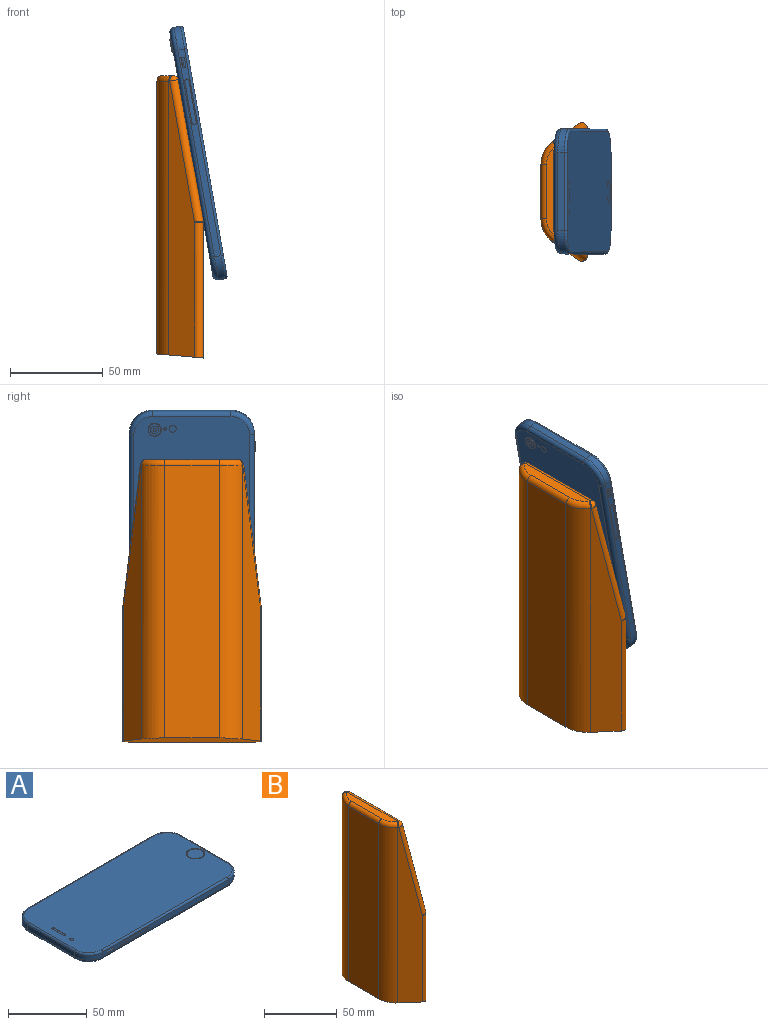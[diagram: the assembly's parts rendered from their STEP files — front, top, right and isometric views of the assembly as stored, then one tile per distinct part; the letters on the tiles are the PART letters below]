
ASSEMBLY  parts=2 mates=1
PART A: 109 faces, bbox 140.3x69.5x8.2 mm
  f0: plane 1.73x1.71mm, normal (0,0,-1), area 2.3mm2, adj f1,f2
  f1: cylinder r=0.86mm len=1.71mm, axis (0,0,-1), area 0mm2, adj f0,f2
  f2: plane 4.33x4.27mm, normal (0,0,-1), area 12mm2, adj f0,f1,f44
  f3: plane 5.31x0.85mm, normal (0,-1,0), area 4.4mm2, adj f7,f8,f9,f10,f11,f12,f13,f14
  f4: plane 10.67x10.67mm, normal (0,0,1), area 89.4mm2, adj f17
  f5: plane 2.46x2.46mm, normal (0,0,1), area 4.8mm2, adj f18
  f6: plane 11.48x1.4mm, normal (0,0,1), area 15.6mm2, adj f19,f20,f21,f22
  f7: cylinder r=0.23mm len=1.75mm, axis (0,-1,0), area 0.6mm2, adj f3,f8,f14,f23
  f8: plane 1.75x0.39mm, normal (-1,0,0), area 0.7mm2, adj f3,f7,f9,f23
  f9: cylinder r=0.23mm len=1.75mm, axis (0,-1,0), area 0.6mm2, adj f3,f8,f10,f23
  f10: plane 4.85x1.75mm, normal (0,0,-1), area 8.5mm2, adj f3,f9,f11,f23
  f11: cylinder r=0.23mm len=1.75mm, axis (0,-1,0), area 0.6mm2, adj f3,f10,f12,f23
  f12: plane 1.75x0.39mm, normal (1,0,0), area 0.7mm2, adj f3,f11,f13,f23
  f13: cylinder r=0.23mm len=1.75mm, axis (0,-1,0), area 0.6mm2, adj f3,f12,f14,f23
  f14: plane 4.85x1.75mm, normal (0,0,1), area 8.5mm2, adj f3,f7,f13,f23
  f15: plane 24.68x2.26mm, normal (0,-1,0), area 54.6mm2, adj f24,f25,f26,f27
  f16: plane 8.81x2.9mm, normal (1,0,0), area 23.7mm2, adj f37,f38,f39,f40
  f17: torus R=5.87mm, axis (0,0,1), area 19.8mm2, adj f4,f43
  f18: cylinder r=1.23mm len=2.46mm, axis (0,0,1), area 0mm2, adj f5,f43
  f19: torus R=0.9mm, axis (0,0,-1), area 0.8mm2, adj f6,f20,f22,f43
  f20: cylinder r=0.2mm len=10.08mm, axis (0,-1,0), area 3.2mm2, adj f6,f19,f21,f43
  f21: torus R=0.9mm, axis (0,0,-1), area 0.8mm2, adj f6,f20,f22,f43
  f22: cylinder r=0.2mm len=10.08mm, axis (0,1,0), area 3.2mm2, adj f6,f19,f21,f43
  f23: plane 5.51x1.89mm, normal (0,-1,0), area 6mm2, adj f7,f8,f9,f10,f11,f12,f13,f14
  f24: cylinder r=0.08mm len=22.42mm, axis (-1,0,0), area 2.7mm2, adj f15,f25,f27,f53
  f25: torus R=1.13mm, axis (0,1,0), area 0.4mm2, adj f15,f24,f26,f54
  f26: cylinder r=0.08mm len=22.42mm, axis (1,0,0), area 2.7mm2, adj f15,f25,f27,f55
  f27: torus R=1.13mm, axis (0,1,0), area 0.4mm2, adj f15,f24,f26,f56
  f28: plane 3.3x3.3mm, normal (1,0,0), area 8.6mm2, adj f60
  f29: plane 1.22x1.22mm, normal (1,0,0), area 1.2mm2, adj f61
  f30: plane 1.22x1.22mm, normal (1,0,0), area 1.2mm2, adj f62
  f31: plane 1.22x1.22mm, normal (1,0,0), area 1.2mm2, adj f63
  f32: plane 1.22x1.22mm, normal (1,0,0), area 1.2mm2, adj f64
  f33: plane 1.22x1.22mm, normal (1,0,0), area 1.2mm2, adj f65
  f34: plane 1.19x1.19mm, normal (1,0,0), area 1.1mm2, adj f66
  f35: plane 1.19x1.19mm, normal (1,0,0), area 1.1mm2, adj f67
  f36: plane 1.14x1.14mm, normal (1,0,0), area 1mm2, adj f68
  f37: plane 7.71x5.92mm, normal (0,0,1), area 45.6mm2, adj f16,f38,f40,f69
  f38: cylinder r=1.45mm len=7.71mm, axis (-1,0,0), area 35.1mm2, adj f16,f37,f39,f70
  f39: plane 7.71x5.92mm, normal (0,0,-1), area 45.6mm2, adj f16,f38,f40,f71
  f40: cylinder r=1.45mm len=7.71mm, axis (-1,0,0), area 35.1mm2, adj f16,f37,f39,f72
  f41: plane 1.22x1.22mm, normal (1,0,0), area 1.2mm2, adj f73
  f42: plane 11.58x2.61mm, normal (0,1,0), area 28.7mm2, adj f75,f76,f77,f78
  f43: plane 135.69x64.87mm, normal (0,0,1), area 8558.8mm2, adj f17,f18,f19,f20,f21,f22,f57,f58
  f44: plane 6.71x6.71mm, normal (0,0,-1), area 21mm2, adj f2,f83
  f45: plane 5.05x1.27mm, normal (0,0,-1), area 6.4mm2, adj f23,f46,f52,f84
  f46: cylinder r=0.23mm len=1.27mm, axis (0,1,0), area 0.5mm2, adj f23,f45,f47,f84
  f47: plane 1.44x1.27mm, normal (-1,0,0), area 1.8mm2, adj f23,f46,f48,f84
  f48: cylinder r=0.23mm len=1.27mm, axis (0,1,0), area 0.5mm2, adj f23,f47,f49,f84
  f49: plane 5.05x1.27mm, normal (0,0,1), area 6.4mm2, adj f23,f48,f50,f84
  f50: cylinder r=0.23mm len=1.27mm, axis (0,1,0), area 0.5mm2, adj f23,f49,f51,f84
  f51: plane 1.44x1.27mm, normal (1,0,0), area 1.8mm2, adj f23,f50,f52,f84
  f52: cylinder r=0.23mm len=1.27mm, axis (0,1,0), area 0.5mm2, adj f23,f45,f51,f84
  f53: plane 22.42x0.08mm, normal (0,0,1), area 1.7mm2, adj f24,f54,f56,f84
  f54: cylinder r=1.21mm len=2.41mm, axis (0,1,0), area 0.3mm2, adj f25,f53,f55,f84
  f55: plane 22.42x0.08mm, normal (0,0,-1), area 1.7mm2, adj f26,f54,f56,f84
  f56: cylinder r=1.2mm len=2.4mm, axis (0,1,0), area 0.3mm2, adj f27,f53,f55,f84
  f57: cylinder r=1.27mm len=113.08mm, axis (1,0,0), area 225.6mm2, adj f43,f58,f82,f84
  f58: torus R=11.3mm, axis (0,0,-1), area 38mm2, adj f43,f57,f59,f85
  f59: cylinder r=1.27mm len=42.27mm, axis (0,1,0), area 84.3mm2, adj f43,f58,f74,f86
  f60: cylinder r=1.65mm len=9.53mm, axis (-1,0,0), area 98.8mm2, adj f28,f85,f86
  f61: cylinder r=0.61mm len=1.22mm, axis (-1,0,0), area 1.9mm2, adj f29,f86
  f62: cylinder r=0.61mm len=1.22mm, axis (-1,0,0), area 1.9mm2, adj f30,f86
  f63: cylinder r=0.61mm len=1.22mm, axis (-1,0,0), area 1.9mm2, adj f31,f86
  f64: cylinder r=0.61mm len=1.22mm, axis (-1,0,0), area 1.9mm2, adj f32,f86
  f65: cylinder r=0.61mm len=1.22mm, axis (-1,0,0), area 1.9mm2, adj f33,f86
  f66: cylinder r=0.6mm len=1.19mm, axis (1,0,0), area 0.3mm2, adj f34,f86
  f67: cylinder r=0.6mm len=1.19mm, axis (1,0,0), area 0.3mm2, adj f35,f86
  f68: cylinder r=0.57mm len=3.17mm, axis (-1,0,0), area 11.4mm2, adj f36,f86
  f69: cylinder r=0.23mm len=5.92mm, axis (0,-1,0), area 2.1mm2, adj f37,f70,f72,f86
  f70: torus R=1.68mm, axis (-1,0,0), area 1.7mm2, adj f38,f69,f71,f86
  f71: cylinder r=0.23mm len=5.92mm, axis (0,1,0), area 2.1mm2, adj f39,f70,f72,f86
  f72: torus R=1.68mm, axis (-1,0,0), area 1.7mm2, adj f40,f69,f71,f86
  f73: cylinder r=0.61mm len=1.22mm, axis (-1,0,0), area 1.9mm2, adj f41,f86,f87
  f74: torus R=11.3mm, axis (0,0,-1), area 38mm2, adj f43,f59,f79,f87
  f75: cylinder r=1.3mm len=2.61mm, axis (0,-1,0), area 0.9mm2, adj f42,f76,f78,f88
  f76: plane 8.98x0.23mm, normal (0,0,-1), area 2.1mm2, adj f42,f75,f77,f88
  f77: cylinder r=1.3mm len=2.61mm, axis (0,-1,0), area 0.9mm2, adj f42,f76,f78,f88
  f78: plane 8.98x0.23mm, normal (0,0,1), area 2.1mm2, adj f42,f75,f77,f88
  f79: cylinder r=1.27mm len=113.08mm, axis (-1,0,0), area 225.6mm2, adj f43,f74,f80,f88
  f80: torus R=11.3mm, axis (0,0,-1), area 38mm2, adj f43,f79,f81,f89
  f81: cylinder r=1.27mm len=42.27mm, axis (0,-1,0), area 84.3mm2, adj f43,f80,f82,f90
  f82: torus R=11.3mm, axis (0,0,-1), area 38mm2, adj f43,f57,f81,f91
  f83: torus R=3.35mm, axis (0,0,-1), area 7mm2, adj f44,f96
  f84: plane 113.08x3.63mm, normal (0,-1,0), area 341.8mm2, adj f45,f46,f47,f48,f49,f50,f51,f52
  f85: cylinder r=12.57mm len=12.57mm, axis (0,0,1), area 71.2mm2, adj f58,f60,f84,f86,f98
  f86: plane 42.27x3.63mm, normal (1,0,0), area 107.6mm2, adj f59,f60,f61,f62,f63,f64,f65,f66
  f87: cylinder r=12.57mm len=12.57mm, axis (0,0,1), area 70.6mm2, adj f73,f74,f86,f88,f100
  f88: plane 113.08x3.63mm, normal (0,1,0), area 382mm2, adj f75,f76,f77,f78,f79,f87,f89,f101
  f89: cylinder r=12.57mm len=12.57mm, axis (0,0,1), area 71.7mm2, adj f80,f88,f90,f102
  f90: plane 42.27x3.63mm, normal (-1,0,0), area 153.5mm2, adj f81,f89,f91,f103
  f91: cylinder r=12.57mm len=12.57mm, axis (0,0,1), area 71.7mm2, adj f82,f84,f90,f104
  f92: plane 22.28x10.98mm, normal (0,0,-1), area 37.9mm2, adj f93,f105
  f93: cylinder r=11.14mm len=22.28mm, axis (0,0,-1), area 0.2mm2, adj f92,f106,f108
  f94: plane 3.84x3.83mm, normal (0,0,-1), area 11.4mm2, adj f106
  f95: plane 1.47x1.46mm, normal (0,0,-1), area 1.6mm2, adj f106
  f96: cylinder r=3.56mm len=7.11mm, axis (0,0,-1), area 12.5mm2, adj f83,f106
  f97: cylinder r=2.54mm len=113.08mm, axis (-1,0,0), area 451.2mm2, adj f84,f98,f104,f106
  f98: torus R=10.03mm, axis (0,0,1), area 73mm2, adj f85,f97,f99,f106
  f99: cylinder r=2.54mm len=42.27mm, axis (0,-1,0), area 168.6mm2, adj f86,f98,f100,f106
  f100: torus R=10.03mm, axis (0,0,1), area 73mm2, adj f87,f99,f101,f106
  f101: cylinder r=2.54mm len=113.08mm, axis (1,0,0), area 451.2mm2, adj f88,f100,f102,f106
  f102: torus R=10.03mm, axis (0,0,1), area 73mm2, adj f89,f101,f103,f106
  f103: cylinder r=2.54mm len=42.27mm, axis (0,1,0), area 168.6mm2, adj f90,f102,f104,f106
  f104: torus R=10.03mm, axis (0,0,1), area 73mm2, adj f91,f97,f103,f106
  f105: cylinder r=11.35mm len=22.28mm, axis (0,0,-1), area 0.1mm2, adj f92,f107,f108
  f106: plane 133.16x62.35mm, normal (0,0,-1), area 7968.8mm2, adj f93,f94,f95,f96,f97,f98,f99,f100
  f107: plane 22.28x9.18mm, normal (0,0,-1), area 153.4mm2, adj f105,f108
  f108: plane 22.28x0.01mm, normal (-1,0,0), area 0.2mm2, adj f93,f105,f106,f107
PART B: 26 faces, bbox 26.2x74.5x152.2 mm
  f0: plane 147x29.38mm, normal (-1,0,0), area 4318.9mm2, adj f1,f9,f10,f20
  f1: plane 74.48x25mm, normal (-0.09,0,-1), area 1535.1mm2, adj f0,f4,f7,f8,f9,f10,f11,f16
  f2: plane 76.05x68.48mm, normal (0.98,0,0.17), area 3589.8mm2, adj f5,f14,f15,f21,f22
  f3: plane 49.7x5.59mm, normal (0,0,1), area 244.3mm2, adj f13,f17,f20,f21,f23,f25
  f4: plane 73.14x68.48mm, normal (1,0,0), area 5008.3mm2, adj f1,f11,f15,f16
  f5: cylinder r=17.6mm len=36.04mm, axis (0.98,0,0.17), area 873.6mm2, adj f2,f6
  f6: plane 35.2x34.67mm, normal (0.98,0,0.17), area 973.1mm2, adj f5
  f7: plane 148.77x13.88mm, normal (-0.57,0.82,0), area 1888.3mm2, adj f1,f9,f11,f13,f14
  f8: plane 148.77x13.88mm, normal (-0.57,-0.82,0), area 1888.3mm2, adj f1,f10,f16,f22,f25
  f9: cylinder r=15mm len=147.56mm, axis (0,0,-1), area 2119.7mm2, adj f0,f1,f7,f17
  f10: cylinder r=15mm len=147.56mm, axis (0,0,1), area 2119.7mm2, adj f0,f1,f8,f23
  f11: cylinder r=3mm len=73.14mm, axis (0,0,1), area 477.6mm2, adj f1,f4,f7,f12
  f12: sphere r=3mm, area 3mm2, adj f11,f14,f15
  f13: cylinder r=3mm len=3mm, axis (-0.82,-0.57,0), area 2.7mm2, adj f3,f7,f17,f18
  f14: cylinder r=3mm len=76.68mm, axis (-0.17,-0.12,0.98), area 506.6mm2, adj f2,f7,f12,f18
  f15: cylinder r=3mm len=68.48mm, axis (0,-1,0), area 35.9mm2, adj f2,f4,f12,f19
  f16: cylinder r=3mm len=73.14mm, axis (0,0,-1), area 477.6mm2, adj f1,f4,f8,f19
  f17: torus R=12mm, axis (0,0,1), area 62.9mm2, adj f3,f9,f13,f20
  f18: sphere r=3mm, area 16.6mm2, adj f13,f14,f21
  f19: sphere r=3mm, area 3mm2, adj f15,f16,f22
  f20: cylinder r=3mm len=29.38mm, axis (0,1,0), area 138.5mm2, adj f0,f3,f17,f23
  f21: cylinder r=3mm len=49.7mm, axis (0,1,0), area 208.2mm2, adj f2,f3,f18,f24
  f22: cylinder r=3mm len=76.68mm, axis (0.17,-0.12,-0.98), area 506.6mm2, adj f2,f8,f19,f24
  f23: torus R=12mm, axis (0,0,1), area 62.9mm2, adj f3,f10,f20,f25
  f24: sphere r=3mm, area 16.6mm2, adj f21,f22,f25
  f25: cylinder r=3mm len=3mm, axis (0.82,-0.57,0), area 2.7mm2, adj f3,f8,f23,f24
PLACE A rot(axis=(0,1,0),80deg) t=(-25.17,41.73,181.29)mm
PLACE B t=(-6.76,7.89,3.48)mm fixed
MATE fastened B.f2 <-> A.f106  axis (0.98,0,0.17) through (-13,7.89,112.31)mm
